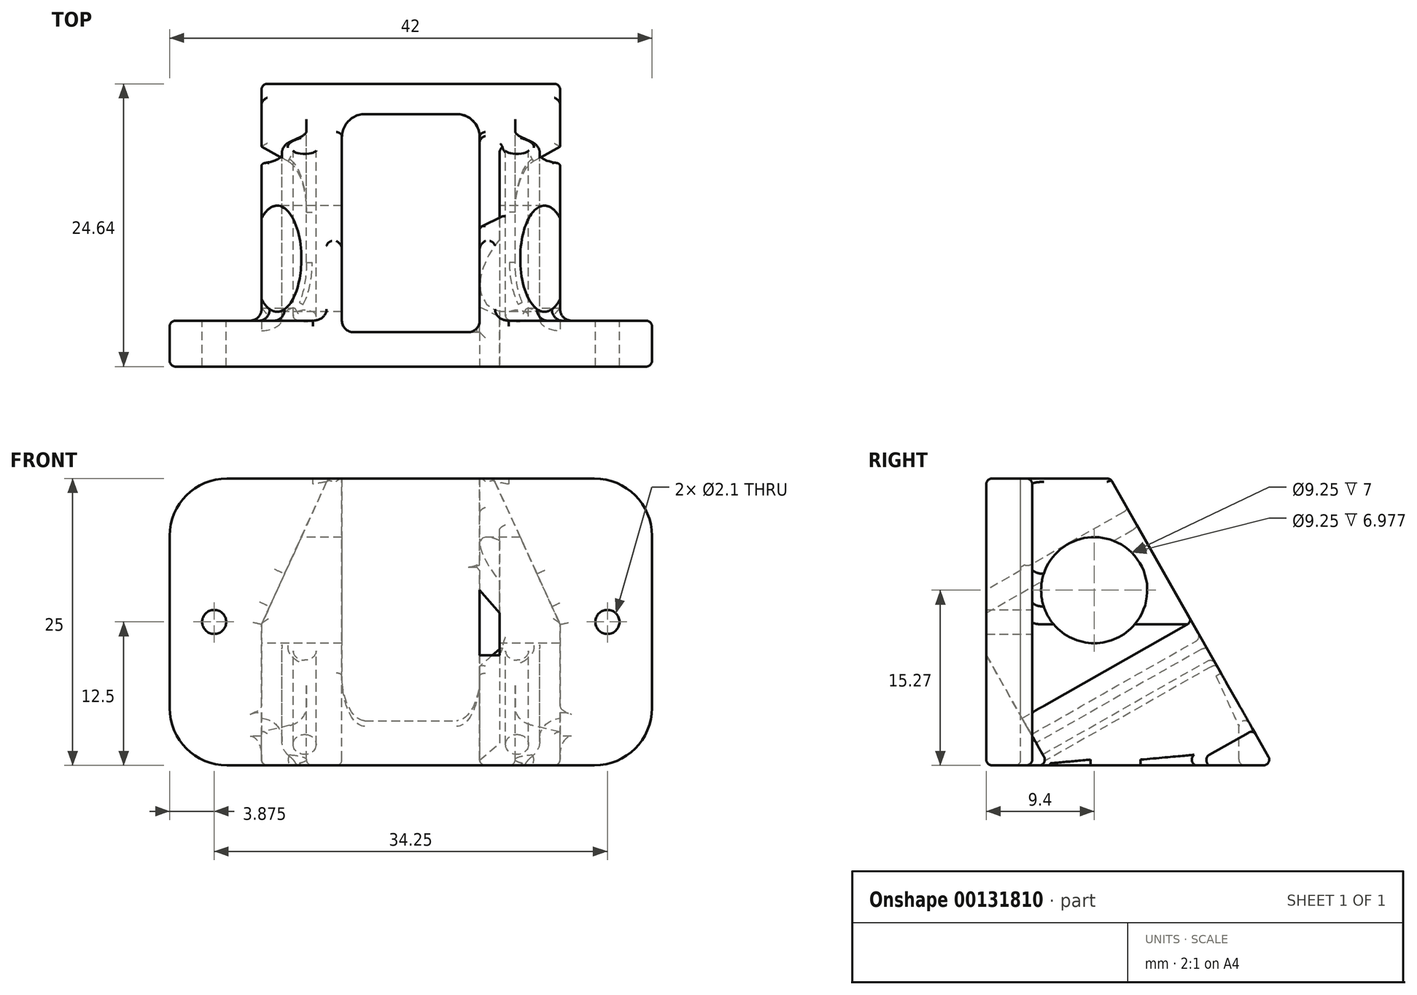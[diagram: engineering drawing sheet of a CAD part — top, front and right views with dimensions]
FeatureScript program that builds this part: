
annotation { "Feature Type Name" : "Feature", "Feature Type Description" : "" }
export const myFeature = defineFeature(function(context is Context, id is Id, definition is map)
    precondition{}
    {
        {
            var Q0;
            Q0=qCreatedBy(makeId("Top.planeOp"),FACE);
            var sketch = newSketch(context, id + "F0", { "sketchPlane" : qUnion([Q0])});
            skLineSegment(sketch, "E0.bottom", {"start": v(21, 12.5) * mm, "end": v(-21, 12.5) * mm});
            skLineSegment(sketch, "E0.top", {"start": v(21, -12.5) * mm, "end": v(-21, -12.5) * mm});
            skLineSegment(sketch, "E0.left", {"start": v(21, 12.5) * mm, "end": v(21, -12.5) * mm});
            skLineSegment(sketch, "E0.right", {"start": v(-21, 12.5) * mm, "end": v(-21, -12.5) * mm});
            skPoint(sketch, "E0.middle", {"position": v(0, 0) * mm});
            skSolve(sketch);
        }
        {
            var Q0;
            Q0=makeQuery(id+"F0.imprint","IMPRINT",FACE,{"disambiguationData":[TD([[makeQuery(id+"F0.imprint","IMPRINT",EDGE,{"derivedFrom":sQuery(id+"F0.wireOp",EDGE,"E0.bottom")}),1.0]])]});
            extrude(context, id + "F1", {"entities" : qUnion([Q0]), "depth" : 25 * mm});
        }
        {
            var Q0;
            Q0=makeQuery(id+"F1.opExtrude","SWEPT_FACE",FACE,{"disambiguationData":[OSD([sQuery(id+"F0.wireOp",EDGE,"E0.bottom")])]});
            var sketch = newSketch(context, id + "F2", { "sketchPlane" : qUnion([Q0])});
            skLineSegment(sketch, "E1.bottom", {"start": v(-21, 25) * mm, "end": v(-13, 25) * mm});
            skLineSegment(sketch, "E1.top", {"start": v(-21, 0) * mm, "end": v(-13, 0) * mm});
            skLineSegment(sketch, "E1.left", {"start": v(-21, 25) * mm, "end": v(-21, 0) * mm});
            skLineSegment(sketch, "E1.right", {"start": v(-13, 25) * mm, "end": v(-13, 0) * mm});
            skLineSegment(sketch, "E2.MirrorCS", {"start": v(13, 25) * mm, "end": v(13, 0) * mm});
            skLineSegment(sketch, "E3.MirrorCS", {"start": v(21, 25) * mm, "end": v(21, 0) * mm});
            skLineSegment(sketch, "E4.MirrorCS", {"start": v(21, 25) * mm, "end": v(13, 25) * mm});
            skLineSegment(sketch, "E5.MirrorCS", {"start": v(21, 0) * mm, "end": v(13, 0) * mm});
            skSolve(sketch);
        }
        {
            var Q0;
            Q0 = qSketchRegion(id + "F2", true);
            extrude(context, id + "F3", {"entities" : qUnion([Q0]), "operationType" : NewBodyOperationType.REMOVE, "oppositeDirection" : true, "depth" : 21 * mm});
        }
        {
            var Q0;
            Q0=makeQuery(id+"F3.boolean.opBoolean","COPY",FACE,{"derivedFrom":makeQuery(id+"F3.opExtrude","SWEPT_FACE",FACE,{"disambiguationData":[OSD([sQuery(id+"F2.wireOp",EDGE,"E2.MirrorCS")])]})});
            var sketch = newSketch(context, id + "F4", { "sketchPlane" : qUnion([Q0])});
            skLineSegment(sketch, "E6", {"start": v(-12.5, 0) * mm, "end": v(1.7, 25) * mm});
            skLineSegment(sketch, "E7", {"start": v(1.7, 25) * mm, "end": v(-12.5, 25) * mm});
            skLineSegment(sketch, "E8", {"start": v(-12.5, 25) * mm, "end": v(-12.5, 0) * mm});
            skSolve(sketch);
        }
        {
            var Q0;
            Q0 = qSketchRegion(id + "F4", true);
            extrude(context, id + "F5", {"entities" : qUnion([Q0]), "operationType" : NewBodyOperationType.REMOVE, "endBound" : BoundingType.UP_TO_NEXT, "oppositeDirection" : true, "depth" : 25 * mm});
        }
        {
            var Q0;
            Q0=makeQuery(id+"F1.opExtrude","CAP_FACE",FACE,{"disambiguationData":[OSD([sQuery(id+"F0.wireOp",EDGE,"E0.bottom"),sQuery(id+"F0.wireOp",EDGE,"E0.top"),sQuery(id+"F0.wireOp",EDGE,"E0.left"),sQuery(id+"F0.wireOp",EDGE,"E0.right")])],"isStart":false});
            var sketch = newSketch(context, id + "F6", { "sketchPlane" : qUnion([Q0])});
            skLineSegment(sketch, "E9.bottom", {"start": v(6, 9.5) * mm, "end": v(-6, 9.5) * mm});
            skLineSegment(sketch, "E9.top", {"start": v(6, -9.5) * mm, "end": v(-6, -9.5) * mm});
            skLineSegment(sketch, "E9.left", {"start": v(6, 9.5) * mm, "end": v(6, -9.5) * mm});
            skLineSegment(sketch, "E9.right", {"start": v(-6, 9.5) * mm, "end": v(-6, -9.5) * mm});
            skPoint(sketch, "E9.middle", {"position": v(0, 0) * mm});
            skSolve(sketch);
        }
        {
            var Q0;
            Q0 = qSketchRegion(id + "F6", true);
            extrude(context, id + "F7", {"entities" : qUnion([Q0]), "operationType" : NewBodyOperationType.REMOVE, "oppositeDirection" : true, "depth" : 30 * mm});
        }
        {
            var Q0;
            Q0=makeQuery(id+"F5.boolean.opBoolean","COPY",FACE,{"derivedFrom":makeQuery(id+"F5.opExtrude","SWEPT_FACE",FACE,{"disambiguationData":[OSD([sQuery(id+"F4.wireOp",EDGE,"E6")])]})});
            var sketch = newSketch(context, id + "F8", { "sketchPlane" : qUnion([Q0])});
            skCircle(sketch, "E10", {"center": v(-9.25, 5.58) * mm, "radius": 1 * mm});
            skLineSegment(sketch, "E11", {"start": v(-13, 8.2) * mm, "end": v(-11.23, 8.2) * mm});
            skLineSegment(sketch, "E12", {"start": v(-11.23, 8.2) * mm, "end": v(-11.23, 5.02) * mm});
            skLineSegment(sketch, "E13", {"start": v(-11.23, 5.02) * mm, "end": v(-9.09, 2.98) * mm});
            skLineSegment(sketch, "E14", {"start": v(-9.09, 2.98) * mm, "end": v(-9.09, -1.56) * mm});
            skLineSegment(sketch, "E15", {"start": v(-9.09, -1.56) * mm, "end": v(-13, -2.62) * mm});
            skLineSegment(sketch, "E16", {"start": v(-13, -2.62) * mm, "end": v(-13, 8.2) * mm});
            skCircle(sketch, "E17.MirrorC", {"center": v(9.25, 5.58) * mm, "radius": 1 * mm});
            skLineSegment(sketch, "E18.MirrorCS", {"start": v(13, 8.2) * mm, "end": v(11.23, 8.2) * mm});
            skLineSegment(sketch, "E19.MirrorCS", {"start": v(11.23, 8.2) * mm, "end": v(11.23, 5.02) * mm});
            skLineSegment(sketch, "E20.MirrorCS", {"start": v(11.23, 5.02) * mm, "end": v(9.09, 2.98) * mm});
            skLineSegment(sketch, "E21.MirrorCS", {"start": v(9.09, 2.98) * mm, "end": v(9.09, -1.56) * mm});
            skLineSegment(sketch, "E22.MirrorCS", {"start": v(13, -2.62) * mm, "end": v(13, 8.2) * mm});
            skLineSegment(sketch, "E23.MirrorCS", {"start": v(9.09, -1.56) * mm, "end": v(13, -2.62) * mm});
            skLineSegment(sketch, "E24.bottom", {"start": v(-6, 3.72) * mm, "end": v(-7.74, 3.72) * mm});
            skLineSegment(sketch, "E24.top", {"start": v(-6, 19.72) * mm, "end": v(-7.74, 19.72) * mm});
            skLineSegment(sketch, "E24.left", {"start": v(-6, 3.72) * mm, "end": v(-6, 19.72) * mm});
            skLineSegment(sketch, "E24.right", {"start": v(-7.74, 3.72) * mm, "end": v(-7.74, 19.72) * mm});
            skSolve(sketch);
        }
        {
            var Q0;
            Q0 = qSketchRegion(id + "F8", true);
            extrude(context, id + "F9", {"entities" : qUnion([Q0]), "operationType" : NewBodyOperationType.REMOVE, "oppositeDirection" : true, "depth" : 17 * mm});
        }
        {
            var Q0;
            {var subQ0=sQuery(id+"F2.wireOp",EDGE,"E2.MirrorCS");var subQ5=sQuery(id+"F8.wireOp",EDGE,"E18.MirrorCS");Q0=makeQuery(id+"F9.boolean.opBoolean","SPLIT",FACE,{"disambiguationData":[TD([makeQuery(id+"F9.opExtrude","SWEPT_FACE",FACE,{"disambiguationData":[OSD([subQ5])]})])],"derivedFrom":makeQuery(id+"F3.boolean.opBoolean","COPY",FACE,{"derivedFrom":makeQuery(id+"F3.opExtrude","SWEPT_FACE",FACE,{"disambiguationData":[OSD([subQ0])]})})});}
            var sketch = newSketch(context, id + "F10", { "sketchPlane" : qUnion([Q0])});
            skCircle(sketch, "E25", {"center": v(3.1, 15.27) * mm, "radius": 4.62 * mm});
            skSolve(sketch);
        }
        {
            var Q0;
            Q0 = qSketchRegion(id + "F10", true);
            extrude(context, id + "F11", {"entities" : qUnion([Q0]), "operationType" : NewBodyOperationType.REMOVE, "oppositeDirection" : true, "depth" : 40 * mm});
        }
        {
            var Q0;
            Q0=makeQuery(id+"F3.boolean.opBoolean","COPY",FACE,{"derivedFrom":makeQuery(id+"F3.opExtrude","CAP_FACE",FACE,{"disambiguationData":[OSD([sQuery(id+"F2.wireOp",EDGE,"E1.bottom"),sQuery(id+"F2.wireOp",EDGE,"E1.top"),sQuery(id+"F2.wireOp",EDGE,"E1.left"),sQuery(id+"F2.wireOp",EDGE,"E1.right")])],"isStart":false})});
            var sketch = newSketch(context, id + "F12", { "sketchPlane" : qUnion([Q0])});
            skPoint(sketch, "E26", {"position": v(-17.12, 12.5) * mm});
            skPoint(sketch, "E27.MirrorP", {"position": v(17.12, 12.5) * mm});
            skSolve(sketch);
        }
        {
            var Q0;
            Q0=sQuery(id+"F12.wireOp",VERTEX,"E27.MirrorP");
            var Q1;
            Q1=sQuery(id+"F12.wireOp",VERTEX,"E26");
            var Q2;
            Q2=makeQuery(id+"F1.opExtrude","SWEPT_BODY",BODY,{"disambiguationData":[OSD([sQuery(id+"F0.wireOp",EDGE,"E0.bottom"),sQuery(id+"F0.wireOp",EDGE,"E0.top"),sQuery(id+"F0.wireOp",EDGE,"E0.left"),sQuery(id+"F0.wireOp",EDGE,"E0.right")])]});
            hole(context, id + "F13", {"style" : HoleStyle.SIMPLE, "endStyle" : HoleEndStyle.THROUGH, "holeDiameter" : 2.1 * mm, "locations" : qUnion([Q0, Q1]), "scope" : qUnion([Q2]), "isTappedThrough" : true});
        }
        {
            var Q0;
            Q0=qCreatedBy(makeId("Front.planeOp"),FACE);
            var sketch = newSketch(context, id + "F14", { "sketchPlane" : qUnion([Q0])});
            skLineSegment(sketch, "E28", {"start": v(13.1, 12.05) * mm, "end": v(7.2, 25) * mm});
            skLineSegment(sketch, "E29", {"start": v(7.2, 25) * mm, "end": v(13.16, 25) * mm});
            skLineSegment(sketch, "E30", {"start": v(13.16, 25) * mm, "end": v(13.1, 12.05) * mm});
            skLineSegment(sketch, "E31.MirrorCS", {"start": v(-13.1, 12.05) * mm, "end": v(-7.2, 25) * mm});
            skLineSegment(sketch, "E32.MirrorCS", {"start": v(-13.16, 25) * mm, "end": v(-13.1, 12.05) * mm});
            skLineSegment(sketch, "E33.MirrorCS", {"start": v(-7.2, 25) * mm, "end": v(-13.16, 25) * mm});
            skSolve(sketch);
        }
        {
            var Q0;
            Q0 = qSketchRegion(id + "F14", true);
            extrude(context, id + "F15", {"entities" : qUnion([Q0]), "operationType" : NewBodyOperationType.REMOVE, "endBound" : BoundingType.SYMMETRIC, "depth" : 17 * mm});
        }
        {
            var Q0;
            Q0=makeQuery(id+"F1.opExtrude","CAP_EDGE",EDGE,{"disambiguationData":[OSD([sQuery(id+"F0.wireOp",EDGE,"E0.right")])],"isStart":false});
            var Q1;
            Q1=makeQuery(id+"F1.opExtrude","CAP_EDGE",EDGE,{"disambiguationData":[OSD([sQuery(id+"F0.wireOp",EDGE,"E0.right")])],"isStart":true});
            var Q2;
            Q2=makeQuery(id+"F1.opExtrude","CAP_EDGE",EDGE,{"disambiguationData":[OSD([sQuery(id+"F0.wireOp",EDGE,"E0.left")])],"isStart":false});
            var Q3;
            Q3=makeQuery(id+"F1.opExtrude","CAP_EDGE",EDGE,{"disambiguationData":[OSD([sQuery(id+"F0.wireOp",EDGE,"E0.left")])],"isStart":true});
            fillet(context, id + "F16", {"entities" : qUnion([Q0, Q1, Q2, Q3]), "radius" : 5 * mm, "tangentPropagation" : true, "allowEdgeOverflow" : false});
        }
        {
            var Q0;
            Q0=makeQuery(id+"F9.boolean.opBoolean","COPY",EDGE,{"derivedFrom":makeQuery(id+"F9.opExtrude","SWEPT_EDGE",EDGE,{"disambiguationData":[OSD([sQuery(id+"F8.wireOp",EDGE,"E12"),sQuery(id+"F8.wireOp",EDGE,"E13")])]})});
            var Q1;
            Q1=makeQuery(id+"F9.boolean.opBoolean","COPY",EDGE,{"derivedFrom":makeQuery(id+"F9.opExtrude","SWEPT_EDGE",EDGE,{"disambiguationData":[OSD([sQuery(id+"F8.wireOp",EDGE,"E13"),sQuery(id+"F8.wireOp",EDGE,"E14")])]})});
            var Q2;
            Q2=makeQuery(id+"F9.boolean.opBoolean","COPY",EDGE,{"derivedFrom":makeQuery(id+"F9.opExtrude","SWEPT_EDGE",EDGE,{"disambiguationData":[OSD([sQuery(id+"F8.wireOp",EDGE,"E11"),sQuery(id+"F8.wireOp",EDGE,"E12")])]})});
            var Q3;
            Q3=makeQuery(id+"F9.boolean.opBoolean","COPY",EDGE,{"derivedFrom":makeQuery(id+"F9.opExtrude","SWEPT_EDGE",EDGE,{"disambiguationData":[OSD([sQuery(id+"F8.wireOp",EDGE,"E18.MirrorCS"),sQuery(id+"F8.wireOp",EDGE,"E19.MirrorCS")])]})});
            var Q4;
            Q4=makeQuery(id+"F9.boolean.opBoolean","COPY",EDGE,{"derivedFrom":makeQuery(id+"F9.opExtrude","SWEPT_EDGE",EDGE,{"disambiguationData":[OSD([sQuery(id+"F8.wireOp",EDGE,"E19.MirrorCS"),sQuery(id+"F8.wireOp",EDGE,"E20.MirrorCS")])]})});
            var Q5;
            Q5=makeQuery(id+"F9.boolean.opBoolean","COPY",EDGE,{"derivedFrom":makeQuery(id+"F9.opExtrude","SWEPT_EDGE",EDGE,{"disambiguationData":[OSD([sQuery(id+"F8.wireOp",EDGE,"E20.MirrorCS"),sQuery(id+"F8.wireOp",EDGE,"E21.MirrorCS")])]})});
            var Q6;
            Q6=makeQuery(id+"F9.boolean.opBoolean","COPY",EDGE,{"derivedFrom":makeQuery(id+"F9.opExtrude","SWEPT_EDGE",EDGE,{"disambiguationData":[OSD([sQuery(id+"F8.wireOp",EDGE,"E21.MirrorCS"),sQuery(id+"F8.wireOp",EDGE,"E23.MirrorCS")])]})});
            var Q7;
            Q7=makeQuery(id+"F9.boolean.opBoolean","COPY",EDGE,{"derivedFrom":makeQuery(id+"F9.opExtrude","SWEPT_EDGE",EDGE,{"disambiguationData":[OSD([sQuery(id+"F8.wireOp",EDGE,"E14"),sQuery(id+"F8.wireOp",EDGE,"E15")])]})});
            fillet(context, id + "F17", {"entities" : qUnion([Q0, Q1, Q2, Q3, Q4, Q5, Q6, Q7]), "radius" : 2 * mm, "tangentPropagation" : true, "allowEdgeOverflow" : false});
        }
        {
            var Q0;
            {var subQ0=sQuery(id+"F2.wireOp",EDGE,"E2.MirrorCS");Q0=makeQuery(id+"F9.boolean.opBoolean","SPLIT",EDGE,{"disambiguationData":[TD([makeQuery(id+"F1.opExtrude","CAP_FACE",FACE,{"disambiguationData":[OSD([sQuery(id+"F0.wireOp",EDGE,"E0.bottom"),sQuery(id+"F0.wireOp",EDGE,"E0.top"),sQuery(id+"F0.wireOp",EDGE,"E0.left"),sQuery(id+"F0.wireOp",EDGE,"E0.right")])],"isStart":false}),makeQuery(id+"F3.boolean.opBoolean","COPY",FACE,{"derivedFrom":makeQuery(id+"F3.opExtrude","SWEPT_FACE",FACE,{"disambiguationData":[OSD([subQ0])]})}),makeQuery(id+"F3.boolean.opBoolean","COPY",FACE,{"derivedFrom":makeQuery(id+"F3.opExtrude","CAP_FACE",FACE,{"disambiguationData":[OSD([subQ0,sQuery(id+"F2.wireOp",EDGE,"E3.MirrorCS"),sQuery(id+"F2.wireOp",EDGE,"E4.MirrorCS"),sQuery(id+"F2.wireOp",EDGE,"E5.MirrorCS")])],"isStart":false})}),makeQuery(id+"F9.opExtrude","SWEPT_FACE",FACE,{"disambiguationData":[OSD([sQuery(id+"F8.wireOp",EDGE,"E18.MirrorCS")])]}),makeQuery(id+"F9.opExtrude","SWEPT_FACE",FACE,{"disambiguationData":[OSD([sQuery(id+"F8.wireOp",EDGE,"E22.MirrorCS")])]})])],"derivedFrom":makeQuery(id+"F3.boolean.opBoolean","COPY",EDGE,{"derivedFrom":makeQuery(id+"F3.opExtrude","CAP_EDGE",EDGE,{"disambiguationData":[OSD([subQ0])],"isStart":false})})});}
            var Q1;
            {var subQ0=sQuery(id+"F2.wireOp",EDGE,"E1.right");Q1=makeQuery(id+"F9.boolean.opBoolean","SPLIT",EDGE,{"disambiguationData":[TD([makeQuery(id+"F1.opExtrude","CAP_FACE",FACE,{"disambiguationData":[OSD([sQuery(id+"F0.wireOp",EDGE,"E0.bottom"),sQuery(id+"F0.wireOp",EDGE,"E0.top"),sQuery(id+"F0.wireOp",EDGE,"E0.left"),sQuery(id+"F0.wireOp",EDGE,"E0.right")])],"isStart":false}),makeQuery(id+"F3.boolean.opBoolean","COPY",FACE,{"derivedFrom":makeQuery(id+"F3.opExtrude","CAP_FACE",FACE,{"disambiguationData":[OSD([sQuery(id+"F2.wireOp",EDGE,"E1.bottom"),sQuery(id+"F2.wireOp",EDGE,"E1.top"),sQuery(id+"F2.wireOp",EDGE,"E1.left"),subQ0])],"isStart":false})}),makeQuery(id+"F3.boolean.opBoolean","COPY",FACE,{"derivedFrom":makeQuery(id+"F3.opExtrude","SWEPT_FACE",FACE,{"disambiguationData":[OSD([subQ0])]})}),makeQuery(id+"F9.opExtrude","SWEPT_FACE",FACE,{"disambiguationData":[OSD([sQuery(id+"F8.wireOp",EDGE,"E11")])]}),makeQuery(id+"F9.opExtrude","SWEPT_FACE",FACE,{"disambiguationData":[OSD([sQuery(id+"F8.wireOp",EDGE,"E16")])]})])],"derivedFrom":makeQuery(id+"F3.boolean.opBoolean","COPY",EDGE,{"derivedFrom":makeQuery(id+"F3.opExtrude","CAP_EDGE",EDGE,{"disambiguationData":[OSD([subQ0])],"isStart":false})})});}
            var Q2;
            Q2=makeQuery(id+"F15.boolean.opBoolean","COPY",EDGE,{"derivedFrom":makeQuery(id+"F15.opExtrude","CAP_EDGE",EDGE,{"disambiguationData":[OSD([sQuery(id+"F14.wireOp",EDGE,"E31.MirrorCS")])],"isStart":false})});
            var Q3;
            Q3=makeQuery(id+"F15.boolean.opBoolean","COPY",EDGE,{"derivedFrom":makeQuery(id+"F15.opExtrude","CAP_EDGE",EDGE,{"disambiguationData":[OSD([sQuery(id+"F14.wireOp",EDGE,"E28")])],"isStart":false})});
            var Q4;
            {var subQ0=sQuery(id+"F0.wireOp",EDGE,"E0.bottom");var subQ1=sQuery(id+"F4.wireOp",EDGE,"E6");Q4=makeQuery(id+"F7.boolean.opBoolean","SPLIT",EDGE,{"disambiguationData":[TD([makeQuery(id+"F3.boolean.opBoolean","COPY",FACE,{"derivedFrom":makeQuery(id+"F3.opExtrude","SWEPT_FACE",FACE,{"disambiguationData":[OSD([sQuery(id+"F2.wireOp",EDGE,"E1.right")])]})})])],"derivedFrom":makeQuery(id+"F5.boolean.opBoolean","COPY",EDGE,{"derivedFrom":makeQuery(id+"F5.opExtrude","SWEPT_EDGE",EDGE,{"disambiguationData":[OSD([subQ0,sQuery(id+"F2.wireOp",EDGE,"E2.MirrorCS"),sQuery(id+"F2.wireOp",EDGE,"E4.MirrorCS"),subQ1,sQuery(id+"F4.wireOp",EDGE,"E7")])]})})});}
            var Q5;
            {var subQ0=sQuery(id+"F0.wireOp",EDGE,"E0.bottom");var subQ1=sQuery(id+"F2.wireOp",EDGE,"E2.MirrorCS");var subQ2=sQuery(id+"F4.wireOp",EDGE,"E6");Q5=makeQuery(id+"F7.boolean.opBoolean","SPLIT",EDGE,{"disambiguationData":[TD([makeQuery(id+"F3.boolean.opBoolean","COPY",FACE,{"derivedFrom":makeQuery(id+"F3.opExtrude","SWEPT_FACE",FACE,{"disambiguationData":[OSD([subQ1])]})})])],"derivedFrom":makeQuery(id+"F5.boolean.opBoolean","COPY",EDGE,{"derivedFrom":makeQuery(id+"F5.opExtrude","SWEPT_EDGE",EDGE,{"disambiguationData":[OSD([subQ0,subQ1,sQuery(id+"F2.wireOp",EDGE,"E4.MirrorCS"),subQ2,sQuery(id+"F4.wireOp",EDGE,"E7")])]})})});}
            var Q6;
            Q6=makeQuery(id+"F7.boolean.opBoolean","COPY",EDGE,{"derivedFrom":makeQuery(id+"F7.opExtrude","SWEPT_EDGE",EDGE,{"disambiguationData":[OSD([sQuery(id+"F6.wireOp",EDGE,"E9.top"),sQuery(id+"F6.wireOp",EDGE,"E9.right")])]})});
            var Q7;
            {var subQ0=sQuery(id+"F6.wireOp",EDGE,"E9.left");var subQ1=sQuery(id+"F6.wireOp",EDGE,"E9.top");Q7=makeQuery(id+"F9.boolean.opBoolean","SPLIT",EDGE,{"disambiguationData":[TD([makeQuery(id+"F1.opExtrude","CAP_FACE",FACE,{"disambiguationData":[OSD([sQuery(id+"F0.wireOp",EDGE,"E0.bottom"),sQuery(id+"F0.wireOp",EDGE,"E0.top"),sQuery(id+"F0.wireOp",EDGE,"E0.left"),sQuery(id+"F0.wireOp",EDGE,"E0.right")])],"isStart":false}),makeQuery(id+"F7.boolean.opBoolean","COPY",FACE,{"derivedFrom":makeQuery(id+"F7.opExtrude","SWEPT_FACE",FACE,{"disambiguationData":[OSD([subQ1])]})}),makeQuery(id+"F7.boolean.opBoolean","COPY",FACE,{"derivedFrom":makeQuery(id+"F7.opExtrude","SWEPT_FACE",FACE,{"disambiguationData":[OSD([subQ0])]})}),makeQuery(id+"F9.opExtrude","SWEPT_FACE",FACE,{"disambiguationData":[OSD([sQuery(id+"F8.wireOp",EDGE,"E24.top")])]}),makeQuery(id+"F9.opExtrude","SWEPT_FACE",FACE,{"disambiguationData":[OSD([sQuery(id+"F8.wireOp",EDGE,"E24.left")])]})])],"derivedFrom":makeQuery(id+"F7.boolean.opBoolean","COPY",EDGE,{"derivedFrom":makeQuery(id+"F7.opExtrude","SWEPT_EDGE",EDGE,{"disambiguationData":[OSD([subQ1,subQ0])]})})});}
            var Q8;
            {var subQ0=sQuery(id+"F8.wireOp",EDGE,"E22.MirrorCS");var subQ1=sQuery(id+"F2.wireOp",EDGE,"E2.MirrorCS");Q8=makeQuery(id+"F9.boolean.opBoolean","SPLIT",EDGE,{"disambiguationData":[TD([makeQuery(id+"F1.opExtrude","CAP_FACE",FACE,{"disambiguationData":[OSD([sQuery(id+"F0.wireOp",EDGE,"E0.bottom"),sQuery(id+"F0.wireOp",EDGE,"E0.top"),sQuery(id+"F0.wireOp",EDGE,"E0.left"),sQuery(id+"F0.wireOp",EDGE,"E0.right")])],"isStart":true}),makeQuery(id+"F3.boolean.opBoolean","COPY",FACE,{"derivedFrom":makeQuery(id+"F3.opExtrude","SWEPT_FACE",FACE,{"disambiguationData":[OSD([subQ1])]})}),makeQuery(id+"F3.boolean.opBoolean","COPY",FACE,{"derivedFrom":makeQuery(id+"F3.opExtrude","CAP_FACE",FACE,{"disambiguationData":[OSD([subQ1,sQuery(id+"F2.wireOp",EDGE,"E3.MirrorCS"),sQuery(id+"F2.wireOp",EDGE,"E4.MirrorCS"),sQuery(id+"F2.wireOp",EDGE,"E5.MirrorCS")])],"isStart":false})}),makeQuery(id+"F9.opExtrude","CAP_FACE",FACE,{"disambiguationData":[OSD([sQuery(id+"F8.wireOp",EDGE,"E18.MirrorCS"),sQuery(id+"F8.wireOp",EDGE,"E19.MirrorCS"),sQuery(id+"F8.wireOp",EDGE,"E20.MirrorCS"),sQuery(id+"F8.wireOp",EDGE,"E21.MirrorCS"),subQ0,sQuery(id+"F8.wireOp",EDGE,"E23.MirrorCS")])],"isStart":false}),makeQuery(id+"F9.opExtrude","SWEPT_FACE",FACE,{"disambiguationData":[OSD([subQ0])]})])],"derivedFrom":makeQuery(id+"F3.boolean.opBoolean","COPY",EDGE,{"derivedFrom":makeQuery(id+"F3.opExtrude","CAP_EDGE",EDGE,{"disambiguationData":[OSD([subQ1])],"isStart":false})})});}
            var Q9;
            {var subQ0=sQuery(id+"F8.wireOp",EDGE,"E16");var subQ1=sQuery(id+"F2.wireOp",EDGE,"E1.right");Q9=makeQuery(id+"F9.boolean.opBoolean","SPLIT",EDGE,{"disambiguationData":[TD([makeQuery(id+"F1.opExtrude","CAP_FACE",FACE,{"disambiguationData":[OSD([sQuery(id+"F0.wireOp",EDGE,"E0.bottom"),sQuery(id+"F0.wireOp",EDGE,"E0.top"),sQuery(id+"F0.wireOp",EDGE,"E0.left"),sQuery(id+"F0.wireOp",EDGE,"E0.right")])],"isStart":true}),makeQuery(id+"F3.boolean.opBoolean","COPY",FACE,{"derivedFrom":makeQuery(id+"F3.opExtrude","CAP_FACE",FACE,{"disambiguationData":[OSD([sQuery(id+"F2.wireOp",EDGE,"E1.bottom"),sQuery(id+"F2.wireOp",EDGE,"E1.top"),sQuery(id+"F2.wireOp",EDGE,"E1.left"),subQ1])],"isStart":false})}),makeQuery(id+"F3.boolean.opBoolean","COPY",FACE,{"derivedFrom":makeQuery(id+"F3.opExtrude","SWEPT_FACE",FACE,{"disambiguationData":[OSD([subQ1])]})}),makeQuery(id+"F9.opExtrude","CAP_FACE",FACE,{"disambiguationData":[OSD([sQuery(id+"F8.wireOp",EDGE,"E11"),sQuery(id+"F8.wireOp",EDGE,"E12"),sQuery(id+"F8.wireOp",EDGE,"E13"),sQuery(id+"F8.wireOp",EDGE,"E14"),sQuery(id+"F8.wireOp",EDGE,"E15"),subQ0])],"isStart":false}),makeQuery(id+"F9.opExtrude","SWEPT_FACE",FACE,{"disambiguationData":[OSD([subQ0])]})])],"derivedFrom":makeQuery(id+"F3.boolean.opBoolean","COPY",EDGE,{"derivedFrom":makeQuery(id+"F3.opExtrude","CAP_EDGE",EDGE,{"disambiguationData":[OSD([subQ1])],"isStart":false})})});}
            fillet(context, id + "F18", {"entities" : qUnion([Q0, Q1, Q2, Q3, Q4, Q5, Q6, Q7, Q8, Q9]), "radius" : 1 * mm, "tangentPropagation" : true, "allowEdgeOverflow" : false});
        }
        {
            var Q0;
            Q0=makeQuery(id+"F7.boolean.opBoolean","COPY",EDGE,{"derivedFrom":makeQuery(id+"F7.opExtrude","SWEPT_EDGE",EDGE,{"disambiguationData":[OSD([sQuery(id+"F6.wireOp",EDGE,"E9.bottom"),sQuery(id+"F6.wireOp",EDGE,"E9.right")])]})});
            var Q1;
            Q1=makeQuery(id+"F7.boolean.opBoolean","COPY",EDGE,{"derivedFrom":makeQuery(id+"F7.opExtrude","SWEPT_EDGE",EDGE,{"disambiguationData":[OSD([sQuery(id+"F6.wireOp",EDGE,"E9.bottom"),sQuery(id+"F6.wireOp",EDGE,"E9.left")])]})});
            fillet(context, id + "F19", {"entities" : qUnion([Q0, Q1]), "radius" : 2 * mm, "tangentPropagation" : true, "allowEdgeOverflow" : false});
        }
        {
            var Q0;
            Q0=makeQuery(id+"F9.boolean.opBoolean","COPY",EDGE,{"derivedFrom":makeQuery(id+"F9.opExtrude","SWEPT_EDGE",EDGE,{"disambiguationData":[OSD([sQuery(id+"F8.wireOp",EDGE,"E24.bottom"),sQuery(id+"F8.wireOp",EDGE,"E24.right")])]})});
            var Q1;
            Q1=makeQuery(id+"F9.boolean.opBoolean","COPY",EDGE,{"derivedFrom":makeQuery(id+"F9.opExtrude","SWEPT_EDGE",EDGE,{"disambiguationData":[OSD([sQuery(id+"F8.wireOp",EDGE,"E24.top"),sQuery(id+"F8.wireOp",EDGE,"E24.right")])]})});
            chamfer(context, id + "F20", {"entities" : qUnion([Q0, Q1]), "width" : 2 * mm, "tangentPropagation" : true});
        }
        {
            var Q0;
            Q0=makeQuery(id+"F5.boolean.opBoolean","COPY",FACE,{"derivedFrom":makeQuery(id+"F5.opExtrude","SWEPT_FACE",FACE,{"disambiguationData":[OSD([sQuery(id+"F4.wireOp",EDGE,"E6")])]})});
            var Q1;
            Q1=makeQuery(id+"F1.opExtrude","CAP_FACE",FACE,{"disambiguationData":[OSD([sQuery(id+"F0.wireOp",EDGE,"E0.bottom"),sQuery(id+"F0.wireOp",EDGE,"E0.top"),sQuery(id+"F0.wireOp",EDGE,"E0.left"),sQuery(id+"F0.wireOp",EDGE,"E0.right")])],"isStart":true});
            fillet(context, id + "F21", {"entities" : qUnion([Q0, Q1]), "radius" : .5 * mm, "tangentPropagation" : true, "allowEdgeOverflow" : false});
        }
    });
